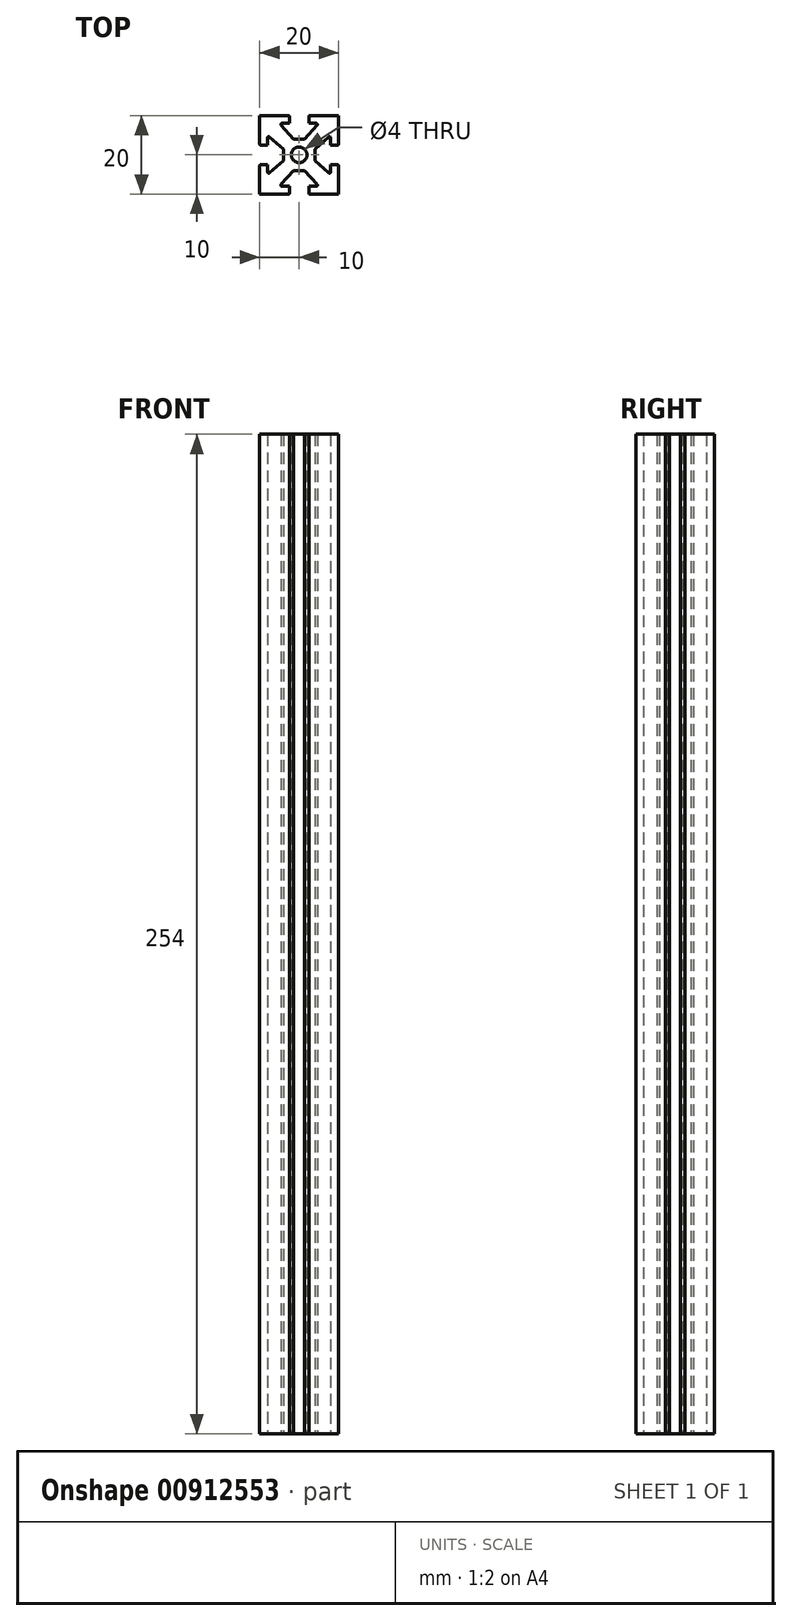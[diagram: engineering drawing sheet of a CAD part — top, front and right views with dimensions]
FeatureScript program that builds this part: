
annotation { "Feature Type Name" : "Feature", "Feature Type Description" : "" }
export const myFeature = defineFeature(function(context is Context, id is Id, definition is map)
    precondition{}
    {
        {
            var Q0;
            Q0=qCreatedBy(makeId("Top.planeOp"),FACE);
            var sketch = newSketch(context, id + "F0", { "sketchPlane" : qUnion([Q0])});
            skLineSegment(sketch, "E0.top", {"start": v(10, 10) * mm, "end": v(2.7, 10) * mm});
            skLineSegment(sketch, "E0.left", {"start": v(10, -10) * mm, "end": v(10, -2.7) * mm});
            skLineSegment(sketch, "E0.right", {"start": v(-10, -10) * mm, "end": v(-10, -2.8) * mm});
            skPoint(sketch, "E0.middle", {"position": v(0, 0) * mm});
            skLineSegment(sketch, "E1", {"start": v(-10, 10) * mm, "end": v(-1.41, 1.41) * mm, "construction": true});
            skLineSegment(sketch, "E2.MirrorCS", {"start": v(-10, 2.5) * mm, "end": v(-10, 10) * mm});
            skLineSegment(sketch, "E3.trimOffspring", {"start": v(-10, 2.7) * mm, "end": v(-10, 10) * mm});
            skLineSegment(sketch, "E4", {"start": v(-10, -10) * mm, "end": v(-1.41, -1.41) * mm, "construction": true});
            skLineSegment(sketch, "E5.MirrorCS", {"start": v(-10, -10) * mm, "end": v(-2.7, -10) * mm});
            skLineSegment(sketch, "E6.trimOffspring", {"start": v(-2.7, -10) * mm, "end": v(-10, -10) * mm});
            skLineSegment(sketch, "E7.MirrorCS", {"start": v(10, -2.7) * mm, "end": v(10, -10) * mm});
            skLineSegment(sketch, "E8.MirrorCS", {"start": v(10, 2.7) * mm, "end": v(10, 10) * mm});
            skCircle(sketch, "E9", {"center": v(0, 0) * mm, "radius": 2 * mm});
            skLineSegment(sketch, "E10", {"start": v(-9.8, 2.5) * mm, "end": v(-8, 2.5) * mm});
            skLineSegment(sketch, "E11", {"start": v(-8, 2.5) * mm, "end": v(-8, 4.33) * mm});
            skLineSegment(sketch, "E12.MirrorCS", {"start": v(-2.5, 8) * mm, "end": v(-4.33, 8) * mm});
            skLineSegment(sketch, "E13.MirrorCS", {"start": v(2.5, -9.8) * mm, "end": v(2.5, -8) * mm});
            skLineSegment(sketch, "E14.MirrorCS", {"start": v(2.5, -8) * mm, "end": v(4.33, -8) * mm});
            skLineSegment(sketch, "E15.MirrorCS", {"start": v(9.8, -2.5) * mm, "end": v(8, -2.5) * mm});
            skLineSegment(sketch, "E16.MirrorCS", {"start": v(8, -2.5) * mm, "end": v(8, -4.33) * mm});
            skLineSegment(sketch, "E17.MirrorCS", {"start": v(9.8, 2.5) * mm, "end": v(8, 2.5) * mm});
            skLineSegment(sketch, "E18.MirrorCS", {"start": v(8, 2.5) * mm, "end": v(8, 4.33) * mm});
            skLineSegment(sketch, "E19.MirrorCS", {"start": v(2.5, 8) * mm, "end": v(4.33, 8) * mm});
            skLineSegment(sketch, "E20.MirrorCS", {"start": v(2.5, 9.8) * mm, "end": v(2.5, 8) * mm});
            skLineSegment(sketch, "E21.MirrorCS", {"start": v(-2.5, -8) * mm, "end": v(-4.33, -8) * mm});
            skLineSegment(sketch, "E22.MirrorCS", {"start": v(-2.5, -9.8) * mm, "end": v(-2.5, -8) * mm});
            skLineSegment(sketch, "E23.MirrorCS", {"start": v(-9.7, -2.5) * mm, "end": v(-8, -2.5) * mm});
            skLineSegment(sketch, "E24.MirrorCS", {"start": v(-8, -2.5) * mm, "end": v(-8, -4.33) * mm});
            skLineSegment(sketch, "E25", {"start": v(7.5, 4.55) * mm, "end": v(4, 1.41) * mm});
            skLineSegment(sketch, "E26", {"start": v(7.5, -4.55) * mm, "end": v(4, -1.41) * mm});
            skLineSegment(sketch, "E27.MirrorCS", {"start": v(4.55, 7.5) * mm, "end": v(1.41, 4) * mm});
            skLineSegment(sketch, "E28.MirrorCS", {"start": v(-4.55, 7.5) * mm, "end": v(-1.41, 4) * mm});
            skLineSegment(sketch, "E29.MirrorCS", {"start": v(-7.5, 4.55) * mm, "end": v(-4, 1.41) * mm});
            skLineSegment(sketch, "E30.MirrorCS", {"start": v(-7.5, -4.55) * mm, "end": v(-4, -1.41) * mm});
            skLineSegment(sketch, "E31.MirrorCS", {"start": v(-4.55, -7.5) * mm, "end": v(-1.41, -4) * mm});
            skLineSegment(sketch, "E32.MirrorCS", {"start": v(4.55, -7.5) * mm, "end": v(1.41, -4) * mm});
            skLineSegment(sketch, "E33", {"start": v(-4, 1.41) * mm, "end": v(-4, -1.41) * mm});
            skLineSegment(sketch, "E34", {"start": v(-1.41, -4) * mm, "end": v(1.41, -4) * mm});
            skLineSegment(sketch, "E35", {"start": v(4, 1.41) * mm, "end": v(4, -1.41) * mm});
            skLineSegment(sketch, "E36", {"start": v(-1.41, 4) * mm, "end": v(1.41, 4) * mm});
            skPoint(sketch, "E37.visualSharp", {"position": v(-5, 8) * mm});
            skArc(sketch, "E37.filletArc", {"start": v(-4.33, 8) * mm, "mid": v(-4.6, 7.82) * mm, "end": v(-4.55, 7.5) * mm});
            skPoint(sketch, "E38.visualSharp", {"position": v(5, 8) * mm});
            skArc(sketch, "E38.filletArc", {"start": v(4.55, 7.5) * mm, "mid": v(4.6, 7.82) * mm, "end": v(4.33, 8) * mm});
            skPoint(sketch, "E39.visualSharp", {"position": v(8, 5) * mm});
            skArc(sketch, "E39.filletArc", {"start": v(8, 4.33) * mm, "mid": v(7.82, 4.6) * mm, "end": v(7.5, 4.55) * mm});
            skPoint(sketch, "E40.visualSharp", {"position": v(-8, 5) * mm});
            skArc(sketch, "E40.filletArc", {"start": v(-7.5, 4.55) * mm, "mid": v(-7.82, 4.6) * mm, "end": v(-8, 4.33) * mm});
            skPoint(sketch, "E41.visualSharp", {"position": v(-8, -5) * mm});
            skArc(sketch, "E41.filletArc", {"start": v(-8, -4.33) * mm, "mid": v(-7.82, -4.6) * mm, "end": v(-7.5, -4.55) * mm});
            skPoint(sketch, "E42.visualSharp", {"position": v(-5, -8) * mm});
            skArc(sketch, "E42.filletArc", {"start": v(-4.55, -7.5) * mm, "mid": v(-4.6, -7.82) * mm, "end": v(-4.33, -8) * mm});
            skPoint(sketch, "E43.visualSharp", {"position": v(5, -8) * mm});
            skArc(sketch, "E43.filletArc", {"start": v(4.33, -8) * mm, "mid": v(4.6, -7.82) * mm, "end": v(4.55, -7.5) * mm});
            skPoint(sketch, "E44.visualSharp", {"position": v(8, -5) * mm});
            skArc(sketch, "E44.filletArc", {"start": v(7.5, -4.55) * mm, "mid": v(7.82, -4.6) * mm, "end": v(8, -4.33) * mm});
            skPoint(sketch, "E45.MirrorCS.end.orphan", {"position": v(-10, 5) * mm});
            skPoint(sketch, "E45.MirrorCS.start.orphan", {"position": v(-10, 2.5) * mm});
            skPoint(sketch, "E46.MirrorCS.end.orphan", {"position": v(5, -10) * mm});
            skPoint(sketch, "E46.MirrorCS.start.orphan", {"position": v(2.5, -10) * mm});
            skPoint(sketch, "E47.MirrorCS.end.orphan", {"position": v(10, -5) * mm});
            skPoint(sketch, "E47.MirrorCS.start.orphan", {"position": v(10, -2.5) * mm});
            skPoint(sketch, "E48.MirrorCS.end.orphan", {"position": v(10, -10) * mm});
            skLineSegment(sketch, "E49", {"start": v(2.7, -10) * mm, "end": v(10, -10) * mm});
            skPoint(sketch, "E50.visualSharp", {"position": v(2.5, 10) * mm});
            skArc(sketch, "E50.filletArc", {"start": v(2.7, 10) * mm, "mid": v(2.56, 9.94) * mm, "end": v(2.5, 9.8) * mm});
            skPoint(sketch, "E51.visualSharp", {"position": v(10, 2.5) * mm});
            skArc(sketch, "E51.filletArc", {"start": v(9.8, 2.5) * mm, "mid": v(9.94, 2.56) * mm, "end": v(10, 2.7) * mm});
            skArc(sketch, "E52.filletArc", {"start": v(10, -2.7) * mm, "mid": v(9.94, -2.56) * mm, "end": v(9.8, -2.5) * mm});
            skArc(sketch, "E53.filletArc", {"start": v(2.5, -9.8) * mm, "mid": v(2.56, -9.94) * mm, "end": v(2.7, -10) * mm});
            skPoint(sketch, "E54.visualSharp", {"position": v(-2.5, -10) * mm});
            skArc(sketch, "E54.filletArc", {"start": v(-2.7, -10) * mm, "mid": v(-2.56, -9.94) * mm, "end": v(-2.5, -9.8) * mm});
            skPoint(sketch, "E55.visualSharp", {"position": v(-10, -2.5) * mm});
            skArc(sketch, "E55.filletArc", {"start": v(-9.7, -2.5) * mm, "mid": v(-9.91, -2.59) * mm, "end": v(-10, -2.8) * mm});
            skArc(sketch, "E56.filletArc", {"start": v(-10, 2.7) * mm, "mid": v(-9.94, 2.56) * mm, "end": v(-9.8, 2.5) * mm});
            skLineSegment(sketch, "E57", {"start": v(-2.5, 8) * mm, "end": v(-2.5, 9.8) * mm});
            skLineSegment(sketch, "E58", {"start": v(-10, 10) * mm, "end": v(-2.7, 10) * mm});
            skPoint(sketch, "E59.visualSharp", {"position": v(-2.5, 10) * mm});
            skArc(sketch, "E59.filletArc", {"start": v(-2.5, 9.8) * mm, "mid": v(-2.56, 9.94) * mm, "end": v(-2.7, 10) * mm});
            skLineSegment(sketch, "E60.trimOffspring", {"start": v(1.41, 1.41) * mm, "end": v(10, 10) * mm, "construction": true});
            skLineSegment(sketch, "E61.trimOffspring", {"start": v(1.41, -1.41) * mm, "end": v(10, -10) * mm, "construction": true});
            skLineSegment(sketch, "E62.trimOffspring", {"start": v(-1.41, -1.41) * mm, "end": v(-10, -10) * mm, "construction": true});
            skPoint(sketch, "E63.MirrorCS.start.orphan", {"position": v(10, 10) * mm});
            skPoint(sketch, "E64.trimOffspring.end.orphan", {"position": v(-10, -10) * mm});
            skPoint(sketch, "E65.end.orphan", {"position": v(-8.93, 0) * mm});
            skPoint(sketch, "E65.start.orphan", {"position": v(-9.92, 0) * mm});
            skSolve(sketch);
        }
        {
            var Q0;
            Q0 = qSketchRegion(id + "F0", true);
            extrude(context, id + "F1", {"entities" : qUnion([Q0]), "depth" : 254 * mm, "offsetDistance" : 25 * mm});
        }
    });
